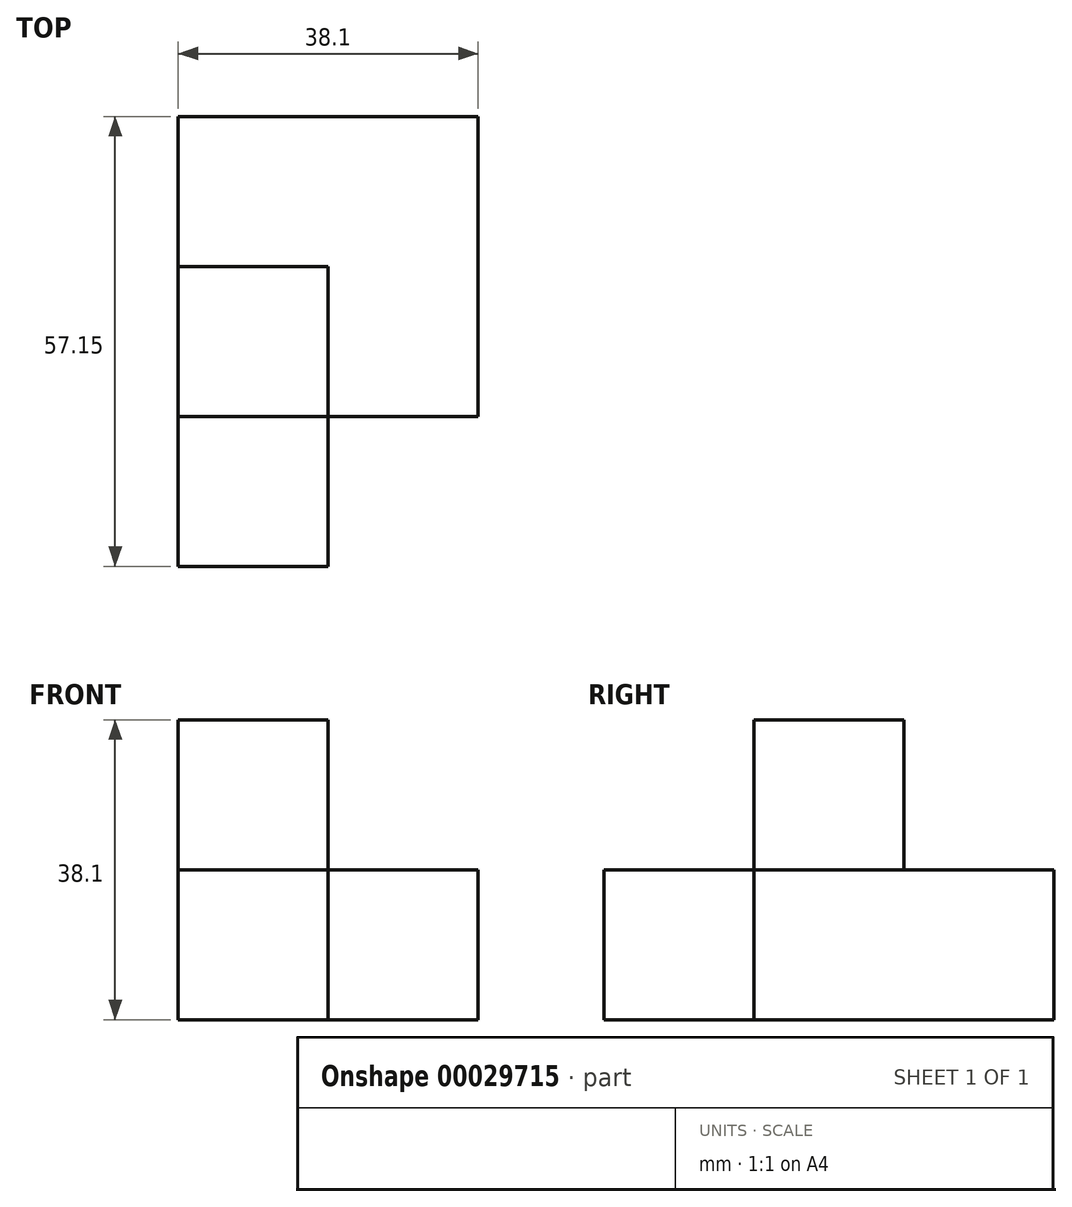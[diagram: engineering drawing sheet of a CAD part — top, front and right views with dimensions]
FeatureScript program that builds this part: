
annotation { "Feature Type Name" : "Feature", "Feature Type Description" : "" }
export const myFeature = defineFeature(function(context is Context, id is Id, definition is map)
    precondition{}
    {
        {
            var Q0;
            Q0=qCreatedBy(makeId("Top.planeOp"),FACE);
            var sketch = newSketch(context, id + "F0", { "sketchPlane" : qUnion([Q0])});
            skLineSegment(sketch, "E0.bottom", {"start": v(-52.22, -57.15) * mm, "end": v(-33.17, -57.15) * mm});
            skLineSegment(sketch, "E0.top", {"start": v(-52.22, 0) * mm, "end": v(-33.17, 0) * mm});
            skLineSegment(sketch, "E0.left", {"start": v(-52.22, -57.15) * mm, "end": v(-52.22, 0) * mm});
            skLineSegment(sketch, "E0.right", {"start": v(-33.17, -57.15) * mm, "end": v(-33.17, 0) * mm});
            skLineSegment(sketch, "E1.bottom", {"start": v(-33.17, 0) * mm, "end": v(-14.12, 0) * mm});
            skLineSegment(sketch, "E1.top", {"start": v(-33.17, -38.1) * mm, "end": v(-14.12, -38.1) * mm});
            skLineSegment(sketch, "E1.left", {"start": v(-33.17, 0) * mm, "end": v(-33.17, -38.1) * mm});
            skLineSegment(sketch, "E1.right", {"start": v(-14.12, 0) * mm, "end": v(-14.12, -38.1) * mm});
            skSolve(sketch);
        }
        {
            var Q0;
            Q0 = qSketchRegion(id + "F0", true);
            extrude(context, id + "F1", {"entities" : qUnion([Q0]), "depth" : 19.05 * mm});
        }
        {
            var Q0;
            Q0=makeQuery(id+"F1.opExtrude","CAP_FACE",FACE,{"disambiguationData":[OSD([sQuery(id+"F0.wireOp",EDGE,"E0.bottom"),sQuery(id+"F0.wireOp",EDGE,"E0.top"),sQuery(id+"F0.wireOp",EDGE,"E0.left"),sQuery(id+"F0.wireOp",EDGE,"E0.right"),sQuery(id+"F0.wireOp",EDGE,"E1.bottom"),sQuery(id+"F0.wireOp",EDGE,"E1.top"),sQuery(id+"F0.wireOp",EDGE,"E1.right")])],"isStart":false});
            var sketch = newSketch(context, id + "F2", { "sketchPlane" : qUnion([Q0])});
            skLineSegment(sketch, "E2.bottom", {"start": v(-33.17, -38.1) * mm, "end": v(-52.22, -38.1) * mm});
            skLineSegment(sketch, "E2.top", {"start": v(-33.17, -19.05) * mm, "end": v(-52.22, -19.05) * mm});
            skLineSegment(sketch, "E2.left", {"start": v(-33.17, -38.1) * mm, "end": v(-33.17, -19.05) * mm});
            skLineSegment(sketch, "E2.right", {"start": v(-52.22, -38.1) * mm, "end": v(-52.22, -19.05) * mm});
            skSolve(sketch);
        }
        {
            var Q0;
            Q0 = qSketchRegion(id + "F2", true);
            extrude(context, id + "F3", {"entities" : qUnion([Q0]), "operationType" : NewBodyOperationType.ADD, "depth" : 19.05 * mm});
        }
    });
